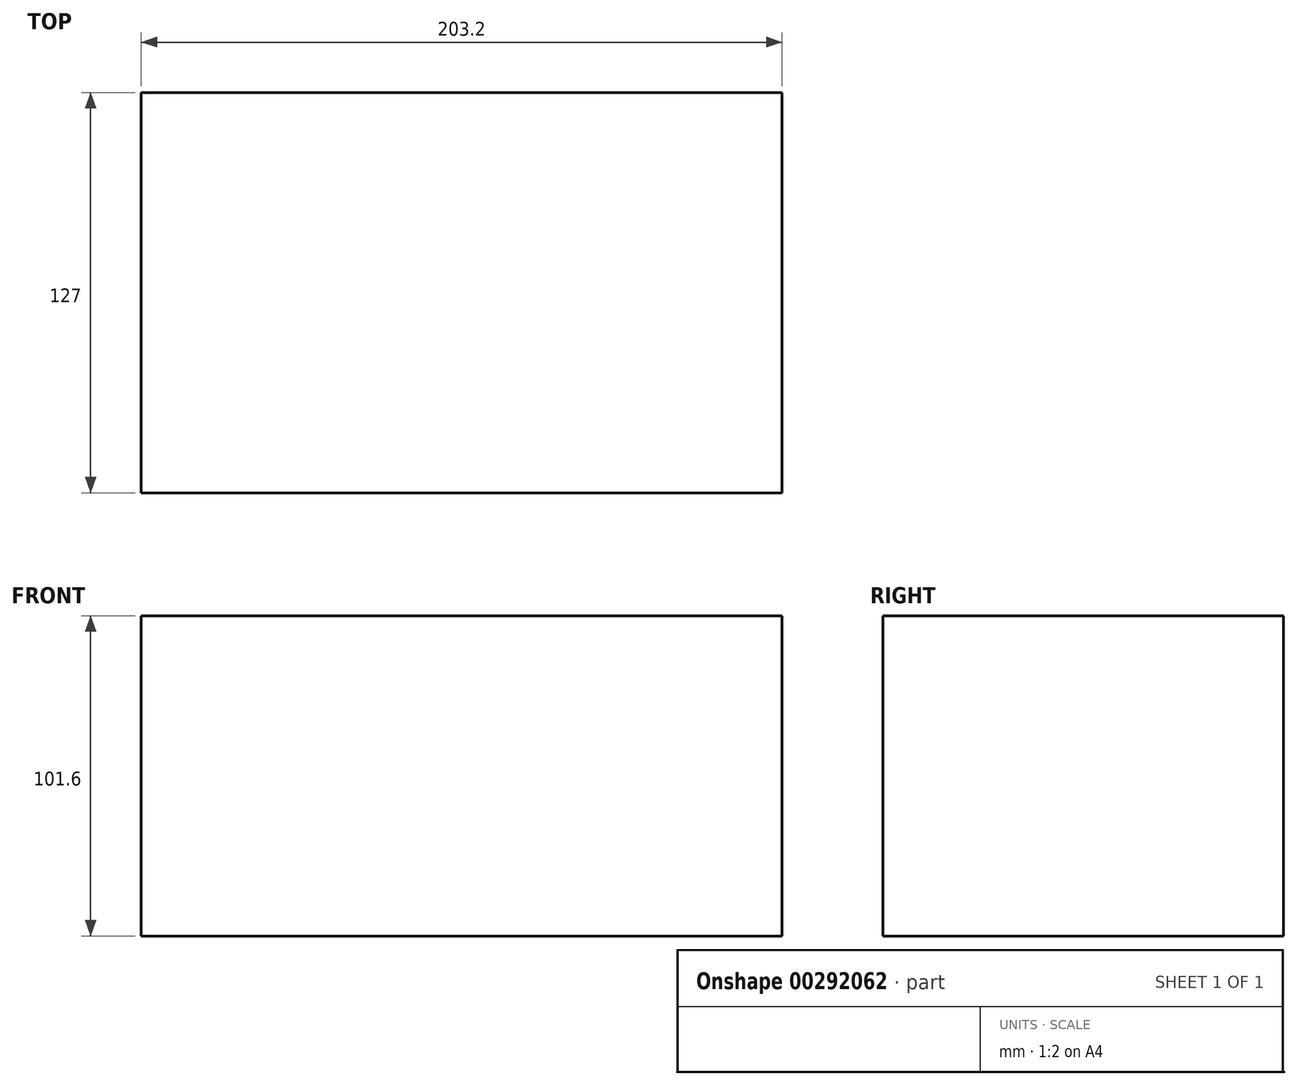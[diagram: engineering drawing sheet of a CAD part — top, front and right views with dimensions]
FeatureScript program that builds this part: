
annotation { "Feature Type Name" : "Feature", "Feature Type Description" : "" }
export const myFeature = defineFeature(function(context is Context, id is Id, definition is map)
    precondition{}
    {
        {
            var Q0;
            Q0=qCreatedBy(makeId("Top.planeOp"),FACE);
            var sketch = newSketch(context, id + "F0", { "sketchPlane" : qUnion([Q0])});
            skLineSegment(sketch, "E0", {"start": v(-67.5, 43.08) * mm, "end": v(135.7, 43.08) * mm});
            skLineSegment(sketch, "E1", {"start": v(135.7, 43.08) * mm, "end": v(135.7, -83.92) * mm});
            skLineSegment(sketch, "E2", {"start": v(135.7, -83.92) * mm, "end": v(-67.5, -83.92) * mm});
            skLineSegment(sketch, "E3", {"start": v(-67.5, -83.92) * mm, "end": v(-67.5, 43.08) * mm});
            skSolve(sketch);
        }
        {
            var Q0;
            Q0=makeQuery(id+"F0.imprint","IMPRINT",FACE,{"disambiguationData":[TD([[makeQuery(id+"F0.imprint","IMPRINT",EDGE,{"derivedFrom":sQuery(id+"F0.wireOp",EDGE,"E0")}),-1.0]])]});
            extrude(context, id + "F1", {"entities" : qUnion([Q0]), "depth" : 101.6 * mm});
        }
    });
